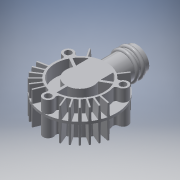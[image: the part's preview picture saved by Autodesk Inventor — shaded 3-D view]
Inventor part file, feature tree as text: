
AUTODESK INVENTOR PART (.ipt)
format: ipt  version: 2016 (Build 200138000, 138)  size: 2,457,600 bytes
history: native  units: in
note: dims shown in document units (in); Inventor stores cm internally (conversion verified against a paired STEP export)
features: sketch x24, extrude x21, pattern_circular x9, plane x4, draft x4, mirror x3, fillet x2, hole x2, revolve x2, other x1, thread x1
ambient origin geometry x8: Origin, YZ Plane, XZ Plane, XY Plane, X Axis, Y Axis, Z Axis, Center Point
bodies: Solid1 (feature_tree)
feature tree (73):
  extrude  "Extrusion1"  Depth=0.05in TaperAngle=0.0deg
  extrude  "Extrusion2"  Depth=1.08in
  extrude  "Extrusion3"  Depth=0.5in
  pattern_circular  "Circular Pattern1"  Count=3 Angle=360.0deg
  plane  "Work Plane2"
  extrude  "Extrusion17"  Depth=0.25in TaperAngle=0.0deg
  extrude  "Extrusion20"  Depth=0.25in
  draft  "FaceDraft5"
  draft  "FaceDraft6"
  fillet  "Fillet6"  Radius=0.125in
  pattern_circular  "Circular Pattern7"  Count=3 Angle=360.0deg
  extrude  "Extrusion21"  Depth=0.25in TaperAngle=360.0deg
  pattern_circular  "Circular Pattern8"  [2 undecoded]
  extrude  "Extrusion22"  Depth=0.25in
  draft  "FaceDraft7"
  draft  "FaceDraft8"
  fillet  "Fillet7"  Radius=0.125in
  pattern_circular  "Circular Pattern9"  [2 undecoded]
  extrude  "Extrusion23"  Depth=0.25in
  pattern_circular  "Circular Pattern10"  [2 undecoded]
  hole  "Hole1"  [1 undecoded]
  pattern_circular  "Circular Pattern11"  [2 undecoded]
  extrude  "Extrusion24"  Depth=0.25in
  plane  "Work Plane5"
  extrude  "Extrusion25"  Depth=0.25in TaperAngle=0.0deg
  hole  "Hole2"  [1 undecoded]
  other  "Work Axis1"
  revolve  "Revolution2"  [1 undecoded]
  pattern_circular  "Circular Pattern2"  [2 undecoded]
  extrude  "Extrusion5"  Depth=0.25in TaperAngle=360.0deg
  extrude  "Extrusion6"  Depth=0.25in
  mirror  "Mirror1"
  mirror  "Mirror2"
  extrude  "Extrusion7"  Depth=0.25in
  extrude  "Extrusion8"  Depth=0.25in TaperAngle=0.0deg
  extrude  "Extrusion9"  Depth=0.25in TaperAngle=360.0deg
  pattern_circular  "Circular Pattern3"  [2 undecoded]
  mirror  "Mirror3"
  extrude  "Extrusion10"  Depth=0.25in
  pattern_circular  "Circular Pattern4"  [2 undecoded]
  extrude  "Extrusion11"  Depth=0.25in
  plane  "Work Plane1"
  extrude  "Extrusion12"  Depth=0.25in TaperAngle=360.0deg
  extrude  "Extrusion13"  Depth=0.25in TaperAngle=0.0deg
  revolve  "Revolution1"  Angle=360.0deg
  extrude  "Extrusion14"  Depth=0.25in
  extrude  "Extrusion16"  Depth=0.25in TaperAngle=360.0deg
  thread  "Thread1"  [1 undecoded]
  sketch  "Sketch1"  dims[d0=1.5in d1=0.05in d2=0.0in]
  sketch  "Sketch2"  dims[d3=1.0in d4=1.08in]
  sketch  "Sketch3"  dims[d5=0.5625in d6=0.5in]
  sketch  "Sketch5"  dims[d7=0.25in d8=0.0in]
  sketch  "Sketch6"  dims[d9=0.05in]
  sketch  "Sketch7"  dims[d10=0.25in d11=0.0in d12=1.1811in d13=360.0deg]
  sketch  "Sketch8"  dims[d20=11.0236in d21=360.0deg d23=0.25in d24=0.0in]
  sketch  "Sketch9"  dims[d25=0.25in d26=0.0in d27=0.5in d28=0.125in d29=0.0in]
  sketch  "Sketch10"  dims[d30=1.0in]
  sketch  "Sketch11"  dims[d31=0.25in d32=0.0in]
  sketch  "Sketch12"  dims[d35=0.25in]
  sketch  "Sketch13"  dims[d36=0.2in]
  sketch  "Sketch14"  dims[d37=0.25in d38=0.0in d39=1.1811in d40=360.0deg]
  sketch  "Sketch15"  dims[d42=0.25in d43=0.0in d44=1.1811in d45=360.0deg]
  sketch  "Sketch17"  dims[d47=0.25in d48=0.0in]
  sketch  "Sketch18"  dims[d49=0.5in]
  sketch  "Sketch20"  dims[d50=0.0625in d51=0.625in d52=0.0in d53=0.0in]
  sketch  "Sketch21"  dims[d54=0.25in d55=0.0in]
  sketch  "Sketch22"  dims[d57=0.1in]
  sketch  "Sketch23"  dims[d58=0.1in]
  sketch  "Sketch24"  dims[d59=0.05in]
  plane  "Work Plane4"
  sketch  "Sketch26"  dims[d60=0.25in]
  sketch  "Sketch27"  dims[d61=0.5in]
  sketch  "Sketch28"  dims[d62=90.0deg d63=0.75in d64=0.0in d67=0.2in d68=0.125in d69=0.0in d70=1.0in d71=0.0in d72=0.25in d76=0.375in d77=0.0in d106=22.5deg d107=0.025in d108=0.025in d109=0.25in d110=0.0in d111=0.0137in d112=0.0137in d113=0.01in d114=12.5984in d115=360.0deg d117=0.1in d118=0.1in d119=0.25in d120=0.0in d121=1.1811in d122=360.0deg d124=0.25in d125=0.0in d126=0.0103in d127=0.0103in d128=0.01in d129=12.5984in d130=360.0deg d132=0.25in d133=0.0in d134=1.1811in d135=360.0deg d137=1.0in d138=1.0in d139=0.129in d140=0.75in d141=0.219in d142=0.112in d143=0.5635in d144=1.0in d145=0.8108in d146=1.1811in d147=360.0deg d149=0.125in d150=0.0in d152=-0.625in d153=0.5in d154=0.5625in d155=0.0in d156=0.313in d157=0.236in d158=0.0246in d159=0.329in d160=0.219in d161=0.112in d162=0.5635in d163=0.25in d164=0.8108in d165=0.125in d166=0.25in d167=90.0deg]
note: 18 required parameter values undecoded (feature->parameter linkage not recoverable at this tier; creation-order binding heuristic only, values carry confidence <= 0.55)